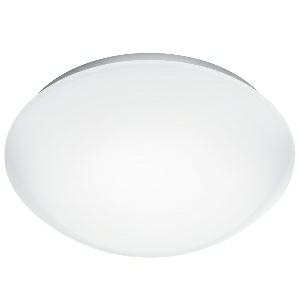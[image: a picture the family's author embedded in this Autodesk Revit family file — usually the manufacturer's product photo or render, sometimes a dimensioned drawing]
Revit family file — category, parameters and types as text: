
# Revit family: rs_pro_led_p3_056117
name_source: partatom
category: Leuchten
revit_build: Autodesk Revit 2016 (Build: 20190508_0715(x64)
units: mm (PartAtom-declared; Revit-internal decimal feet)

## family parameters
Basisbauteil = Fläche
Beim Laden mit Abzugskörper schneiden = Nein
Bemaßung runder Anschluss = Durchmesser verwenden
Gemeinsam genutzt = Nein
Lichtquelle = Nein
Raumberechnungspunkt = Nein
Teiletyp = Normal

## types (1)
- RS PRO LED P3 (1 x , 2310 lm, 4000 K)
    Beschreibung = Dimensions (Ø x H): 400 x 142 mm; Mains power supply: 220 – 240 V / 50 – 60 Hz; Sensor Technology: High frequency; Transmitter power: < 1 mW; HF-system: 5,8 GHz; Output: 20 W; Interconnection: Yes; Type of interconnection: Master/master; Luminous flux: 2310 lm; Colour temperature: 4000 K; Colour variation LED: SDCM3; Colour Rendering Index CRI: 80-89; With lamp: Yes, STEINEL LED system; Lamp: LED cannot be replaced; LED life expectancy (max. °C): 50000 h; Drop in luminous flux in accordance with LM80: L80B10; Base: without; LED cooling system: Passive Thermo Control; With motion detector: Yes; Detection: also through glass, wood and stud walls; Detection angle: 360 °; Angle of aperture: 160 °; Capability of masking out individual segments: Yes; Electronic scalability: Yes; Mechanical scalability: No; Reach, radial: Ø 8 m (50 m²); Reach, tangential: Ø 8 m (50 m²); Continuous light: selectable, 4h; Photo-cell controller: Yes; Twilight setting: 2 – 2000 lx; Time setting: 5 sec – 15 min; Basic light level function: Yes; Basic light level function time: 10/30 min, all night; Soft light start: Yes; Impact resistance: IK03; IP-rating: IP54; Protection class: II; Ambient temperature: 10 – 40 °C; Housing material: Plastic; Cover material: Plastic, opal; Manufacturer's Warranty: 5 years; Settings via: Potentiometers; With remote control: No; Version: Neutral white; PU1, EAN: 4007841056117
    CIE Flux Codes = 39 67 87 85 100
    Color Rendering = 80-89
    Color Temperature = 4000 K
    Frequency = 50 Hz, 60 Hz
    Height = 0 mm  [stored 0 ft]
    Hersteller = Steinel
    Lamp Light Flux = 2310 lm
    Lamp count = 1
    Lampe = 1 x
    Length = 400 mm
    Luminous efficacy = 116 lm/W
    ModVariant = Nein
    Modell = 056117
    Mounting Type = Surface mounted
    Number of Poles = 1
    OnlyDefault = Ja
    Power Factor = 1
    Product Name = RS PRO LED P3
    Product group = Sensor-switched indoor light
    ProductGroupID = 30
    Protection Class = Protection class II
    Protection Degree = IP 54
    RlxData = <blob elided: 38877 chars, md5=a3b00dd8>
    Scheinlast = 20 VA
    Socket = socket
    Standby Power = 0 W
    System Light Flux = 2310 lm
    System Power = 20 W
    Typenbild = produkt1_056117.jpg
    Typenkommentare = Product without accessories
    URL = http://relux.com
    VarID = ---
    Voltage = 0 V
    Vorgabe-Ansicht = 1800 mm
    Weight = 0.00 kg
    Width = 0 mm  [stored 0 ft]

note: [stored X ft] marks values corroborated as IEEE doubles in the binary element streams (Revit-internal decimal feet)

## geometry (parser evidence)
native form markers: Sweep x14
no freeform markers — native parametric forms only
